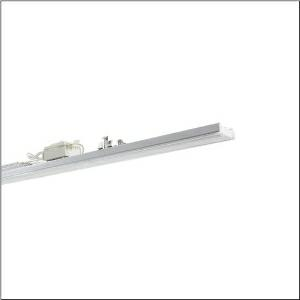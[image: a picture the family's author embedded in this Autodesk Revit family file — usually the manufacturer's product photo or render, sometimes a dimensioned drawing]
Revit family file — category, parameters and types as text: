
# Revit family: licross_r__21_recessed_ho_52te11dn4e5s_c18d
name_source: partatom
category: Lighting Fixtures
units: mm (PartAtom-declared; Revit-internal decimal feet)

## family parameters
Cut with Voids When Loaded = No
Host = Face
Light Source = No
Part Type = Normal
Room Calculation Point = No
Round Connector Dimension = Use Diameter
Shared = No

## types (1)
- --- (1 x LED, 14970 lm, 84.6 W, 4000K)
    Apparent Load = 85 VA
    CIE Flux Codes = 87 95 99 100 100
    Color Rendering = 80
    Color Temperature = 4000K
    Default Elevation = 1800 mm
    Description = Licross® 21 Recessed HO, luminaire insert, of sheet steel, galvanised, coil coated, white, length: 1.500mm, width: 66mm, height: 67mm, LED rated luminous flux: 14.970lm, light colour: 840, control gear: DALI 2, with plug, 5-pole, with phase selection, mains connection: 220..240V, AC, 50/60Hz, rated input power: 85W, halogen-free wiring, primary light control with lens, of plastic, primary optical cover: cover, of PMMA, light emission: direct distribution, primary light characteristic: symmetric, protection rating (complete): IP54, insulation class (complete): insulation class I (protective earthing), certification: CE, ENEC, VDE, UKCA, protection symbol: D if used in an environment with non-conductive dust loads with corresponding accessories, impact resistance: IK06, permissible ambient temperature for indoor applications: -25..+30°C, corresponds to IFS (International Featured Standards) requirements for safety and quality in the food industry, reducing of maximum allowable ambient temperature of 5°C with ceiling mounting, LABS conformity tested according to VDMA 24364:2018-05, packaging unit: 1 piece
    Height = 58 mm
    Lamp = 1 x LED
    Lamp Light Flux = 14970 lm
    Lamp Power = 84.6 W
    Lamp count = 1
    Length = 1500 mm
    Luminous efficacy = 177 lm/W
    Manufacturer = Siteco
    ModVariant = No
    Model = 52TE11DN4E5S
    Mounting Place = Ceiling
    Mounting Type = Pendant
    Number of Poles = 1
    OnlyDefault = Yes
    Power Factor = 1
    Product Name = Licross® 21 Recessed HO
    Product group = luminaire insert
    ProductGroupID = 902
    Protection Class = Protection class I
    Protection Degree = IP 54
    RLX_Detail_Level = 1
    RLX_Emergency_Light_Flux = 0 lm
    RLX_Emergency_Type = 0
    RLX_Emergency_Type_DB = No
    RlxData = <blob elided: 24717 chars, md5=69f35997>
    Socket = socket
    Standby Power = 0 W
    System Light Flux = 14970 lm
    System Power = 85 W
    Type Comments = factory setting: luminous flux: 100 % | dim-lin: 254 | 484 mA
    Type Image = l_1296930.jpg
    URL = http://relux.com
    VarID = @adj_127170
    Voltage = 0 V
    Weight = 0.00 kg
    Width = 66 mm

## geometry (parser evidence)
native form markers: Blend x4, Sweep x10
no freeform markers — native parametric forms only
